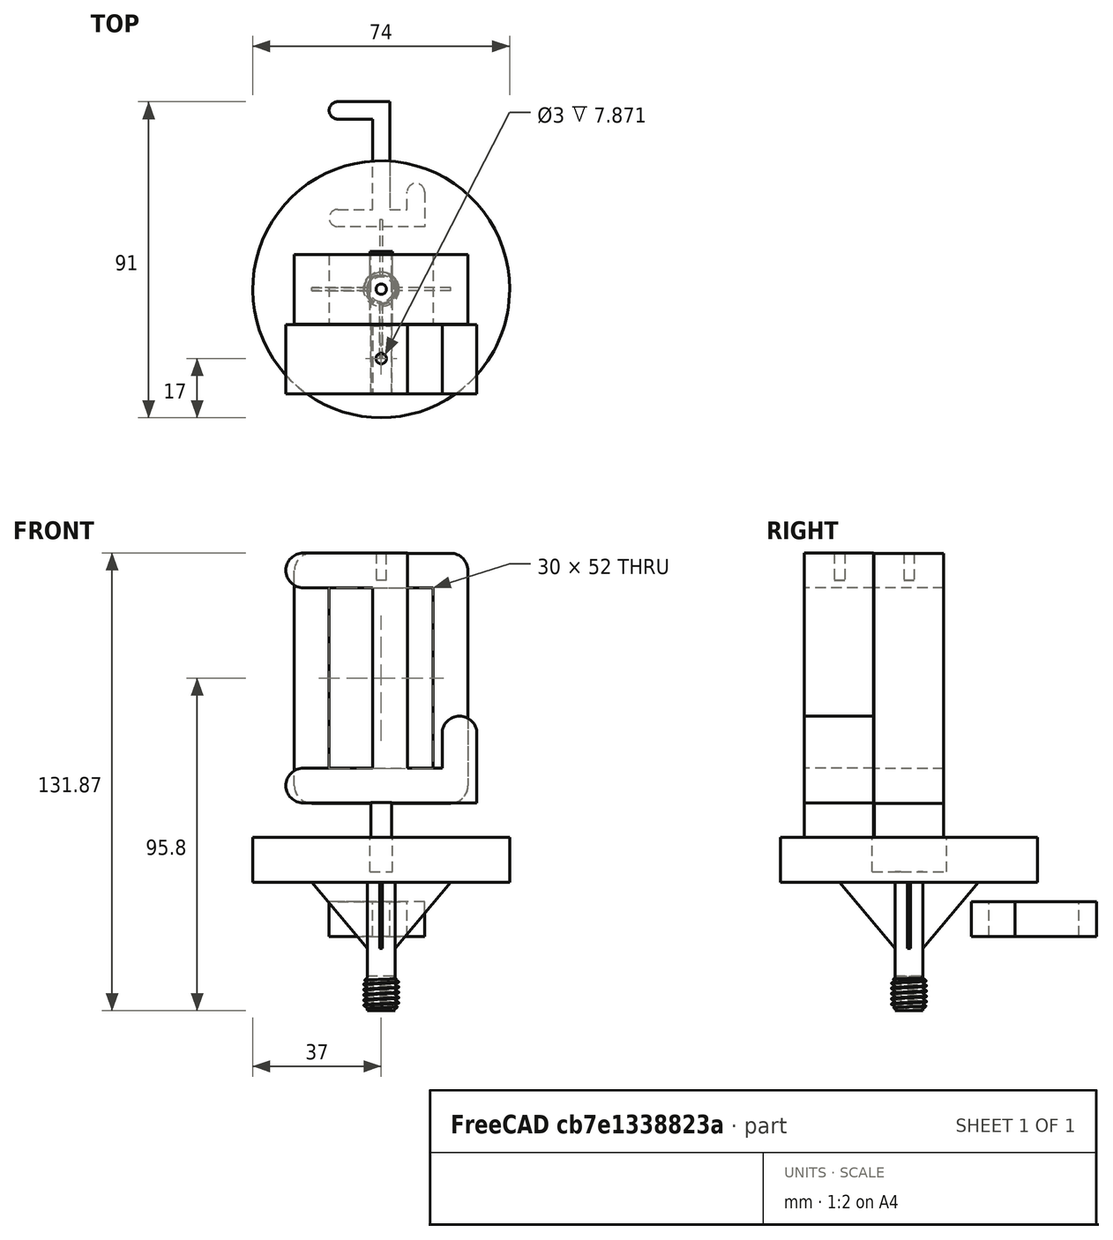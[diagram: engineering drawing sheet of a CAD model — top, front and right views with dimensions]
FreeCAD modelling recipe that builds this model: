
FCSTD DOCUMENT  (FreeCAD 0.20R29603 (Git))
Label: coderdojo_nul_en_een
License: All rights reserved
LicenseURL: http://en.wikipedia.org/wiki/All_rights_reserved
objects: Part::Box×5, Part::Cylinder×4, Sketcher::SketchObject×3, PartDesign::Body×3, Part::FeaturePython×3, Part::MultiFuse×3, Part::Cut×3, PartDesign::Pad×2, Mesh::Feature×2, Part::Chamfer×2
note: 30 computed .brp shape members not serialized (recipe doc carries the construction recipe); baked Part::Feature solids carry a one-line shape summary decoded from their .brp

FEATURE [Sketcher::SketchObject] Sketch002
  AttachmentOffset = pos=(0,0,11.4) rot=(0,0,1;0rad)
  FullyConstrained = true
  MapMode = 5
  Placement = pos=(0,0,11.4) rot=(0,0,1;0rad)
  Support = -> [XY_Plane]
  sketch-geometry (12):
    g0: LineSegment StartX=-7.5 StartY=-23 StartZ=0 EndX=7.5 EndY=-23 EndZ=0
    g1: LineSegment StartX=7.5 StartY=-23 StartZ=0 EndX=7.5 EndY=-49 EndZ=0
    g2: LineSegment StartX=7.5 StartY=-49 StartZ=0 EndX=-7.5 EndY=-49 EndZ=0
    g3: LineSegment StartX=-7.5 StartY=-49 StartZ=0 EndX=-7.5 EndY=-23 EndZ=0
    g4: LineSegment StartX=-10 StartY=-18 StartZ=0 EndX=10 EndY=-18 EndZ=0
    g5: ArcOfCircle CenterX=10 CenterY=-20.5 CenterZ=0 NormalX=0 NormalY=0 NormalZ=1 AngleXU=0 Radius=2.5 StartAngle=9e-16 EndAngle=1.5708
    g6: LineSegment StartX=12.5 StartY=-20.5 StartZ=0 EndX=12.5 EndY=-51.5 EndZ=0
    g7: ArcOfCircle CenterX=10 CenterY=-51.5 CenterZ=0 NormalX=0 NormalY=0 NormalZ=1 AngleXU=0 Radius=2.5 StartAngle=4.71239 EndAngle=6.28319
    g8: LineSegment StartX=10 StartY=-54 StartZ=0 EndX=-10 EndY=-54 EndZ=0
    g9: ArcOfCircle CenterX=-10 CenterY=-51.5 CenterZ=0 NormalX=0 NormalY=0 NormalZ=1 AngleXU=0 Radius=2.5 StartAngle=3.14159 EndAngle=4.71239
    g10: LineSegment StartX=-12.5 StartY=-51.5 StartZ=0 EndX=-12.5 EndY=-20.5 EndZ=0
    g11: ArcOfCircle CenterX=-10 CenterY=-20.5 CenterZ=0 NormalX=0 NormalY=0 NormalZ=1 AngleXU=0 Radius=2.5 StartAngle=1.5708 EndAngle=3.14159
  constraints (31):
    c: Vertical(g1)
    c: Horizontal(g2)
    c: Vertical(g3)
    c: Symmetric(g0,g0,g-2)
    c: Horizontal(g4)
    c: Vertical(g6)
    c: Horizontal(g8)
    c: Tangent(g4,g11) = 1.5708
    c: Tangent(g4,g5) = 1.5708
    c: Tangent(g5,g6) = 1.5708
    c: Tangent(g6,g7) = 1.5708
    c: Tangent(g7,g8) = 1.5708
    c: Tangent(g8,g9) = 1.5708
    c: Tangent(g9,g10) = 1.5708
    c: Tangent(g10,g11) = 1.5708
    c: DistanceX(g9,g6) = 25
    c: Radius(g11) = 2.5
    c: DistanceX(g10,g3) = 5
    c: Vertical(g10)
    c: Coincident(g0,g3)
    c: Coincident(g0,g1)
    c: Coincident(g1,g2)
    c: Coincident(g2,g3)
    c: DistanceY(g8,g2) = 5
    c: DistanceY(g0,g4) = 5
    c: DistanceX(g0,g5) = 5
    c: DistanceY(g7,g4) = 36
    c: DistanceY(g4,g-1) = 18
    c: Equal(g9,g11)
    c: Equal(g11,g5)
    c: Equal(g5,g7)
FEATURE [PartDesign::Pad] Pad
  Direction = (0,0,1)
  Length = 10
  Length2 = 10
  Profile = -> Sketch002
  ReferenceAxis = -> Sketch002 [N_Axis]
  Type = 0
FEATURE [PartDesign::Body] Body
  Group = -> [Sketch002,Pad]
  Origin = -> Origin
  Tip = -> Pad
FEATURE [Part::FeaturePython] Clone  label="Nul"  # Draft clone (typed FeaturePython)
  AttacherType = Attacher::AttachEngine3D
  Fuse = false
  Objects = -> [Body]
  Placement = pos=(0,32.76,157.8) rot=(1,0,0;1.5708rad)
  Scale = (2,2,2)
FEATURE [Sketcher::SketchObject] Sketch
  AttachmentOffset = pos=(0,0,11.4) rot=(0,0,1;0rad)
  FullyConstrained = false
  MapMode = 5
  Placement = pos=(0,0,11.4) rot=(0,0,1;0rad)
  sketch-geometry (12):
    g0: ArcOfCircle CenterX=-12.5 CenterY=51.5 CenterZ=0 NormalX=0 NormalY=0 NormalZ=1 AngleXU=0 Radius=2.5 StartAngle=1.5708 EndAngle=4.71239
    g1: LineSegment StartX=-12.5 StartY=54 StartZ=0 EndX=2.5 EndY=54 EndZ=0
    g2: LineSegment StartX=2.5 StartY=54 StartZ=0 EndX=2.5 EndY=23 EndZ=0
    g3: LineSegment StartX=2.5 StartY=23 StartZ=0 EndX=7.5 EndY=23 EndZ=0
    g4: LineSegment StartX=7.5 StartY=23 StartZ=0 EndX=7.5 EndY=28 EndZ=0
    g5: ArcOfCircle CenterX=10 CenterY=28 CenterZ=0 NormalX=0 NormalY=0 NormalZ=1 AngleXU=0 Radius=2.5 StartAngle=-9e-16 EndAngle=3.14159
    g6: LineSegment StartX=12.5 StartY=28 StartZ=0 EndX=12.5 EndY=18 EndZ=0
    g7: LineSegment StartX=12.5 StartY=18 StartZ=0 EndX=-12.5 EndY=18 EndZ=0
    g8: ArcOfCircle CenterX=-12.5 CenterY=20.5 CenterZ=0 NormalX=0 NormalY=0 NormalZ=1 AngleXU=0 Radius=2.5 StartAngle=1.5708 EndAngle=4.71239
    g9: LineSegment StartX=-12.5 StartY=23 StartZ=0 EndX=-2.5 EndY=23 EndZ=0
    g10: LineSegment StartX=-2.5 StartY=23 StartZ=0 EndX=-2.5 EndY=49 EndZ=0
    g11: LineSegment StartX=-2.5 StartY=49 StartZ=0 EndX=-12.5 EndY=49 EndZ=0
  constraints (31):
    c: Horizontal(g1)
    c: Coincident(g2,g1)
    c: Vertical(g2)
    c: Coincident(g3,g2)
    c: Coincident(g4,g3)
    c: Vertical(g4)
    c: Vertical(g6)
    c: Coincident(g7,g6)
    c: Horizontal(g9)
    c: Coincident(g10,g9)
    c: Vertical(g10)
    c: Coincident(g11,g10)
    c: Horizontal(g11)
    c: Tangent(g0,g1) = 1.5708
    c: Equal(g0,g8)
    c: Equal(g8,g5)
    c: Radius(g0) = 2.5
    c: DistanceX(g3,g3) = 5
    c: Horizontal(g3)
    c: DistanceX(g10,g1) = 5
    c: Equal(g9,g11)
    c: Tangent(g8,g9) = 1.5708
    c: Tangent(g7,g8) = 1.5708
    c: Tangent(g5,g6) = 1.5708
    c: Tangent(g4,g5) = 1.5708
    c: Tangent(g0,g11) = 1.5708
    c: Symmetric(g7,g6,g-2)
    c: Symmetric(g9,g2,g-2)
    c: DistanceY(g6,g1) = 36
    c: DistanceX(g7,g6) = 25
    c: DistanceY(g3,g4) = 5
FEATURE [PartDesign::Body] Body001
  Group = -> [Sketch]
  Origin = -> Origin002
FEATURE [Part::Cylinder] Cylinder  label="Cilinder"
  Angle = 360
  AttacherType = Attacher::AttachEngine3D
  FirstAngle = 0
  Height = 40
  Placement = pos=(0,0,-10) rot=(0,0,1;0rad)
  Radius = 4
  SecondAngle = 0
FEATURE [Part::Box] Box  label="Kubus"
  AttacherType = Attacher::AttachEngine3D
  Height = 10
  Length = 6
  Placement = pos=(-3,-10,40) rot=(0,0,1;0rad)
  Width = 20
FEATURE [Part::Box] Box001  label="Kubus001"
  AttacherType = Attacher::AttachEngine3D
  Height = 10
  Length = 6.5
  Placement = pos=(-3.25,-10.6,30) rot=(0,0,1;0rad)
  Width = 21.5
FEATURE [Part::MultiFuse] Fusion001  label="de_nul"
  Shapes = -> [Box,Clone]
FEATURE [Part::Cylinder] Cylinder001  label="Cilinder001"
  Angle = 360
  AttacherType = Attacher::AttachEngine3D
  FirstAngle = 0
  Height = 10
  Placement = pos=(0,0,114) rot=(0,0,1;0rad)
  Radius = 1.5
  SecondAngle = 0
FEATURE [Part::Cut] Cut001  label="De_nul"
  Base = -> Fusion001
  Tool = -> Cylinder001
FEATURE [Mesh::Feature] Mesh001  label="De_nul.stl"
FEATURE [Part::Cylinder] Cylinder002  label="Cilinder002"
  Angle = 360
  AttacherType = Attacher::AttachEngine3D
  FirstAngle = 0
  Height = 13
  Placement = pos=(0,0,27) rot=(0,0,1;0rad)
  Radius = 37
  SecondAngle = 0
FEATURE [Part::Cut] Cut
  Base = -> Cylinder002
  Tool = -> Box001
FEATURE [Part::Box] Box002  label="Kubus002"
  AttacherType = Attacher::AttachEngine3D
  Height = 20
  Length = 40
  Placement = pos=(-20,-0.4,8) rot=(0,0,1;0rad)
  Width = 0.8
FEATURE [Part::Chamfer] Chamfer
  Base = -> Box002
  Edges = 2 edges: [Edge4 r1=19 r2=16,Edge8 r1=19 r2=16]
FEATURE [Part::Box] Box003  label="Kubus003"
  AttacherType = Attacher::AttachEngine3D
  Height = 20
  Length = 40
  Placement = pos=(-20,-0.4,8) rot=(0,0,1;0rad)
  Width = 0.8
FEATURE [Part::Chamfer] Chamfer001
  Base = -> Box003
  Edges = 2 edges: [Edge4 r1=19 r2=16,Edge8 r1=19 r2=16]
  Placement = pos=(0,0,0) rot=(0,0,1;1.5708rad)
FEATURE [Part::MultiFuse] Fusion  label="Drijver"
  Shapes = -> [Cut,Cylinder,Chamfer,Chamfer001]
FEATURE [Sketcher::SketchObject] Sketch003
  AttachmentOffset = pos=(0,0,11.4) rot=(0,0,1;0rad)
  FullyConstrained = false
  MapMode = 5
  Placement = pos=(0,0,11.4) rot=(0,0,1;0rad)
  Support = -> [XY_Plane006]
  sketch-geometry (12):
    g0: ArcOfCircle CenterX=-12.5 CenterY=51.5 CenterZ=0 NormalX=0 NormalY=0 NormalZ=1 AngleXU=0 Radius=2.5 StartAngle=1.5708 EndAngle=4.71239
    g1: LineSegment StartX=-12.5 StartY=54 StartZ=0 EndX=2.5 EndY=54 EndZ=0
    g2: LineSegment StartX=2.5 StartY=54 StartZ=0 EndX=2.5 EndY=23 EndZ=0
    g3: LineSegment StartX=2.5 StartY=23 StartZ=0 EndX=7.5 EndY=23 EndZ=0
    g4: LineSegment StartX=7.5 StartY=23 StartZ=0 EndX=7.5 EndY=28 EndZ=0
    g5: ArcOfCircle CenterX=10 CenterY=28 CenterZ=0 NormalX=0 NormalY=0 NormalZ=1 AngleXU=0 Radius=2.5 StartAngle=-9e-16 EndAngle=3.14159
    g6: LineSegment StartX=12.5 StartY=28 StartZ=0 EndX=12.5 EndY=18 EndZ=0
    g7: LineSegment StartX=12.5 StartY=18 StartZ=0 EndX=-12.5 EndY=18 EndZ=0
    g8: ArcOfCircle CenterX=-12.5 CenterY=20.5 CenterZ=0 NormalX=0 NormalY=0 NormalZ=1 AngleXU=0 Radius=2.5 StartAngle=1.5708 EndAngle=4.71239
    g9: LineSegment StartX=-12.5 StartY=23 StartZ=0 EndX=-2.5 EndY=23 EndZ=0
    g10: LineSegment StartX=-2.5 StartY=23 StartZ=0 EndX=-2.5 EndY=49 EndZ=0
    g11: LineSegment StartX=-2.5 StartY=49 StartZ=0 EndX=-12.5 EndY=49 EndZ=0
  constraints (31):
    c: Horizontal(g1)
    c: Coincident(g2,g1)
    c: Vertical(g2)
    c: Coincident(g3,g2)
    c: Coincident(g4,g3)
    c: Vertical(g4)
    c: Vertical(g6)
    c: Coincident(g7,g6)
    c: Horizontal(g9)
    c: Coincident(g10,g9)
    c: Vertical(g10)
    c: Coincident(g11,g10)
    c: Horizontal(g11)
    c: Tangent(g0,g1) = 1.5708
    c: Equal(g0,g8)
    c: Equal(g8,g5)
    c: Radius(g0) = 2.5
    c: DistanceX(g3,g3) = 5
    c: Horizontal(g3)
    c: DistanceX(g10,g1) = 5
    c: Equal(g9,g11)
    c: Tangent(g8,g9) = 1.5708
    c: Tangent(g7,g8) = 1.5708
    c: Tangent(g5,g6) = 1.5708
    c: Tangent(g4,g5) = 1.5708
    c: Tangent(g0,g11) = 1.5708
    c: Symmetric(g7,g6,g-2)
    c: Symmetric(g9,g2,g-2)
    c: DistanceY(g6,g1) = 36
    c: DistanceX(g7,g6) = 25
    c: DistanceY(g3,g4) = 5
FEATURE [PartDesign::Pad] Pad001
  Direction = (0,0,1)
  Length = 10
  Length2 = 10
  Profile = -> Sketch003
  ReferenceAxis = -> Sketch003 [N_Axis]
  Type = 0
FEATURE [PartDesign::Body] Body002
  Group = -> [Sketch003,Pad001]
  Origin = -> Origin004
  Tip = -> Pad001
FEATURE [Part::FeaturePython] Clone001  label="Pad002"  # Draft clone (typed FeaturePython)
  AttacherType = Attacher::AttachEngine3D
  Fuse = false
  Objects = -> [Pad001]
  Placement = pos=(2.55872,12.6027,13.8708) rot=(1,0,0;1.5708rad)
  Scale = (2,2,2)
FEATURE [Part::Box] Box004  label="Kubus004"
  AttacherType = Attacher::AttachEngine3D
  Height = 10
  Length = 6
  Placement = pos=(-3,-30.2,40) rot=(0,0,1;0rad)
  Width = 20
FEATURE [Part::MultiFuse] Fusion002  label="de_een"
  Shapes = -> [Clone001,Box004]
FEATURE [Part::Cylinder] Cylinder003  label="Cilinder003"
  Angle = 360
  AttacherType = Attacher::AttachEngine3D
  FirstAngle = 0
  Height = 10
  Placement = pos=(0,-20,114) rot=(0,0,1;0rad)
  Radius = 1.5
  SecondAngle = 0
FEATURE [Part::Cut] Cut002  label="De_een"
  Base = -> Fusion002
  Tool = -> Cylinder003
FEATURE [Mesh::Feature] Mesh002  label="De_een.stl"
FEATURE [Part::FeaturePython] ThreadedRod  label="M10x10-ThreadedRod"  # Fasteners workbench fastener (typed FeaturePython)
  diameter = 10
  diameterCustom = 4
  invert = false
  leftHanded = false
  length = 10
  matchOuter = false
  offset = 0
  pitchCustom = 1
  thread = true
  type = 0
